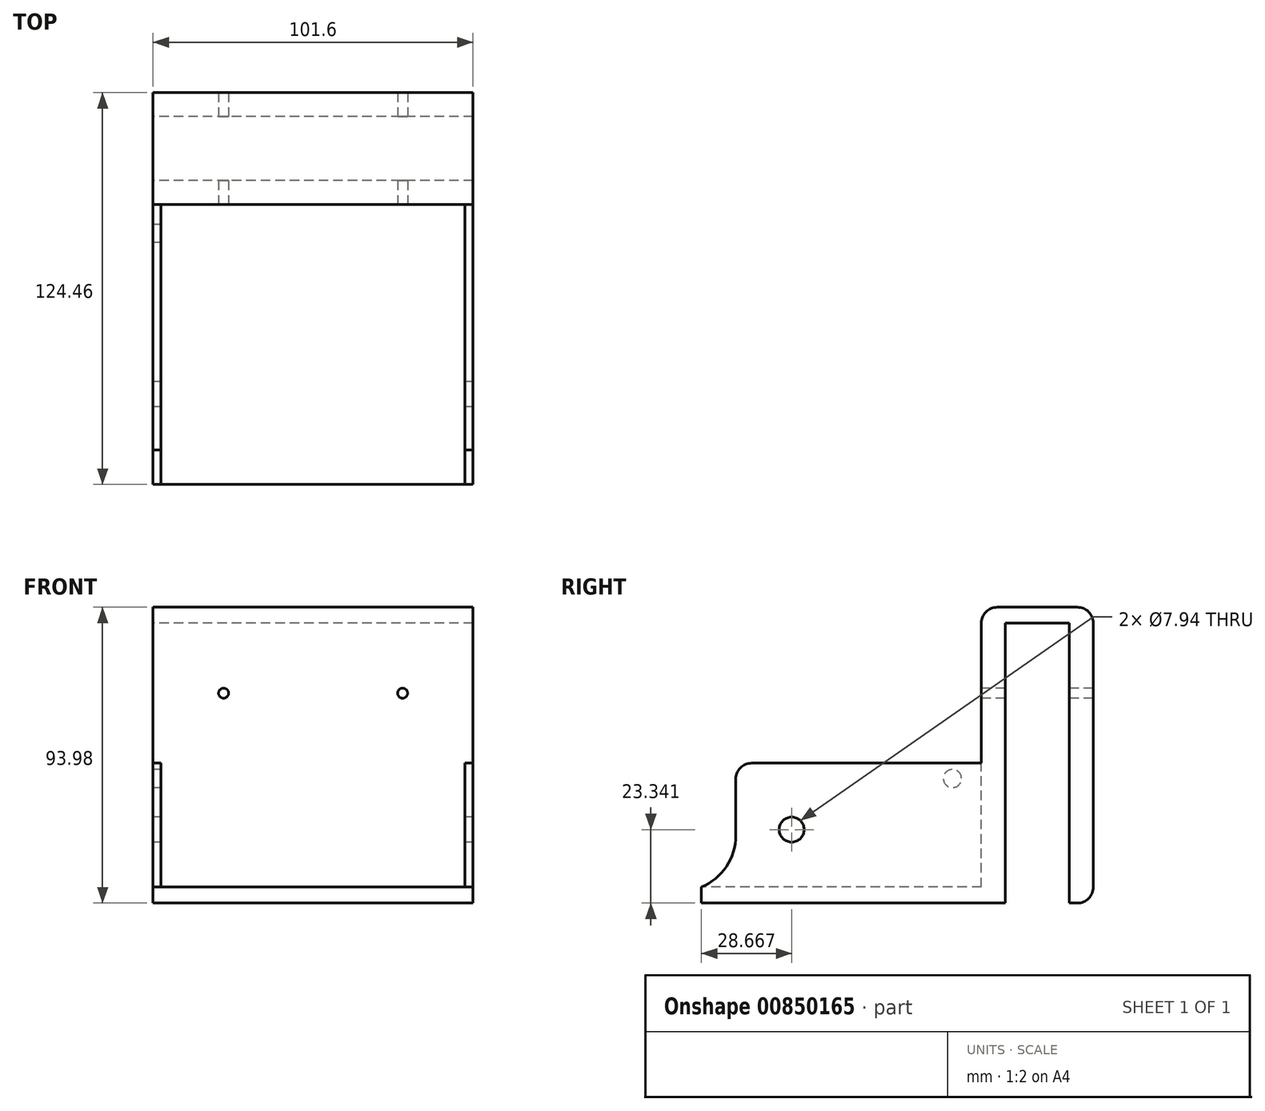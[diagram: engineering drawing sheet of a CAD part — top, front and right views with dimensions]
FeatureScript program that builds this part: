
annotation { "Feature Type Name" : "Feature", "Feature Type Description" : "" }
export const myFeature = defineFeature(function(context is Context, id is Id, definition is map)
    precondition{}
    {
        {
            var Q0;
            Q0=qCreatedBy(makeId("Right.planeOp"),FACE);
            var sketch = newSketch(context, id + "F0", { "sketchPlane" : qUnion([Q0])});
            skLineSegment(sketch, "E0.bottom", {"start": v(-10.16, -44.45) * mm, "end": v(10.16, -44.45) * mm});
            skLineSegment(sketch, "E0.top", {"start": v(-10.16, 44.45) * mm, "end": v(10.16, 44.45) * mm});
            skLineSegment(sketch, "E0.left", {"start": v(-10.16, -44.45) * mm, "end": v(-10.16, 44.45) * mm});
            skLineSegment(sketch, "E0.right", {"start": v(10.16, -44.45) * mm, "end": v(10.16, 44.45) * mm});
            skPoint(sketch, "E0.middle", {"position": v(0, 0) * mm});
            skLineSegment(sketch, "E1.bottom", {"start": v(-17.78, -44.45) * mm, "end": v(17.78, -44.45) * mm});
            skLineSegment(sketch, "E1.top", {"start": v(-17.78, 44.45) * mm, "end": v(17.78, 44.45) * mm});
            skLineSegment(sketch, "E1.left", {"start": v(-17.78, -44.45) * mm, "end": v(-17.78, 44.45) * mm});
            skLineSegment(sketch, "E1.right", {"start": v(17.78, -44.45) * mm, "end": v(17.78, 44.45) * mm});
            skLineSegment(sketch, "E2.top", {"start": v(-17.78, 49.53) * mm, "end": v(17.78, 49.53) * mm});
            skLineSegment(sketch, "E2.left", {"start": v(-17.78, 44.45) * mm, "end": v(-17.78, 49.53) * mm});
            skLineSegment(sketch, "E2.right", {"start": v(17.78, 44.45) * mm, "end": v(17.78, 49.53) * mm});
            skLineSegment(sketch, "E3.bottom", {"start": v(-10.16, -44.45) * mm, "end": v(-106.68, -44.45) * mm});
            skLineSegment(sketch, "E3.top", {"start": v(-10.16, -39.37) * mm, "end": v(-106.68, -39.37) * mm});
            skLineSegment(sketch, "E3.left", {"start": v(-10.16, -44.45) * mm, "end": v(-10.16, -39.37) * mm});
            skLineSegment(sketch, "E3.right", {"start": v(-106.68, -44.45) * mm, "end": v(-106.68, -39.37) * mm});
            skSolve(sketch);
        }
        {
            var Q0;
            {var subQ0=sQuery(id+"F0.wireOp",EDGE,"E0.right");Q0=makeQuery(id+"F0.imprint","IMPRINT",FACE,{"disambiguationData":[TD([[makeQuery(id+"F0.imprint","IMPRINT",EDGE,{"derivedFrom":subQ0}),-1.0]])]});}
            var Q1;
            {var subQ1=sQuery(id+"F0.wireOp",EDGE,"E0.top");Q1=makeQuery(id+"F0.imprint","IMPRINT",FACE,{"disambiguationData":[TD([[makeQuery(id+"F0.imprint","IMPRINT",EDGE,{"derivedFrom":subQ1}),1.0]])]});}
            var Q2;
            {var subQ1=sQuery(id+"F0.wireOp",EDGE,"E0.left");var subQ3=sQuery(id+"F0.wireOp",EDGE,"E3.top");var subQ4=makeQuery(id+"F0.imprint","INTERSECT",VERTEX,{"derivedFrom":[subQ1,subQ3]});Q2=makeQuery(id+"F0.imprint","IMPRINT",FACE,{"disambiguationData":[TD([[makeQuery(id+"F0.imprint","IMPRINT",EDGE,{"disambiguationData":[TD([[subQ4,-1.0]])],"derivedFrom":subQ3}),-1.0]])]});}
            var Q3;
            {var subQ3=sQuery(id+"F0.wireOp",EDGE,"E3.bottom");Q3=makeQuery(id+"F0.imprint","IMPRINT",FACE,{"disambiguationData":[TD([[makeQuery(id+"F0.imprint","IMPRINT",EDGE,{"derivedFrom":subQ3}),-1.0]])]});}
            var Q4;
            {var subQ1=sQuery(id+"F0.wireOp",EDGE,"E0.left");var subQ3=sQuery(id+"F0.wireOp",EDGE,"E3.top");var subQ4=makeQuery(id+"F0.imprint","INTERSECT",VERTEX,{"derivedFrom":[subQ1,subQ3]});Q4=makeQuery(id+"F0.imprint","IMPRINT",FACE,{"disambiguationData":[TD([[makeQuery(id+"F0.imprint","IMPRINT",EDGE,{"disambiguationData":[TD([[subQ4,-1.0]])],"derivedFrom":subQ3}),1.0]])]});}
            extrude(context, id + "F1", {"entities" : qUnion([Q0, Q1, Q2, Q3, Q4]), "depth" : 101.6 * mm, "offsetDistance" : 25.4 * mm});
        }
        {
            var Q0;
            Q0=qCreatedBy(makeId("Front.planeOp"),FACE);
            var sketch = newSketch(context, id + "F2", { "sketchPlane" : qUnion([Q0])});
            skLineSegment(sketch, "E4.0", {"start": v(0, -39.37) * mm, "end": v(0, 49.53) * mm});
            skPoint(sketch, "E5.0", {"position": v(0, 0) * mm});
            skLineSegment(sketch, "E6.0", {"start": v(101.6, -39.37) * mm, "end": v(101.6, 49.53) * mm});
            skLineSegment(sketch, "E7", {"start": v(0, 0) * mm, "end": v(101.6, 0) * mm});
            skPoint(sketch, "E8.0", {"position": v(0, -44.45) * mm});
            skPoint(sketch, "E9.0", {"position": v(101.6, -44.45) * mm});
            skLineSegment(sketch, "E10.bottom", {"start": v(0, 0) * mm, "end": v(2.54, 0) * mm});
            skLineSegment(sketch, "E10.top", {"start": v(0, -44.45) * mm, "end": v(2.54, -44.45) * mm});
            skLineSegment(sketch, "E10.left", {"start": v(0, 0) * mm, "end": v(0, -44.45) * mm});
            skLineSegment(sketch, "E10.right", {"start": v(2.54, 0) * mm, "end": v(2.54, -44.45) * mm});
            skLineSegment(sketch, "E11.bottom", {"start": v(101.6, 0) * mm, "end": v(99.06, 0) * mm});
            skLineSegment(sketch, "E11.top", {"start": v(101.6, -44.45) * mm, "end": v(99.06, -44.45) * mm});
            skLineSegment(sketch, "E11.left", {"start": v(101.6, 0) * mm, "end": v(101.6, -44.45) * mm});
            skLineSegment(sketch, "E11.right", {"start": v(99.06, 0) * mm, "end": v(99.06, -44.45) * mm});
            skSolve(sketch);
        }
        {
            var Q0;
            {Q0=qUnion([makeQuery(id+"F2.imprint","IMPRINT",FACE,{"disambiguationData":[TD([[makeQuery(id+"F2.imprint","IMPRINT",EDGE,{"derivedFrom":sQuery(id+"F2.wireOp",EDGE,"E10.top")}),1.0]])]}),makeQuery(id+"F2.imprint","IMPRINT",FACE,{"disambiguationData":[TD([[makeQuery(id+"F2.imprint","IMPRINT",EDGE,{"derivedFrom":sQuery(id+"F2.wireOp",EDGE,"E11.top")}),-1.0]])]})]);}
            extrude(context, id + "F3", {"entities" : qUnion([Q0]), "operationType" : NewBodyOperationType.ADD, "depth" : 95.76 * mm, "offsetDistance" : 25.4 * mm, "hasSecondDirection" : true, "secondDirectionOppositeDirection" : false, "secondDirectionDepth" : 17.02 * mm});
        }
        {
            var Q0;
            Q0=makeQuery(id+"F3.boolean.opBoolean","INTERSECT",EDGE,{"derivedFrom":[makeQuery(id+"F1.opExtrude","SWEPT_FACE",FACE,{"disambiguationData":[OSD([sQuery(id+"F0.wireOp",EDGE,"E3.top")])]}),makeQuery(id+"F3.opExtrude","CAP_FACE",FACE,{"disambiguationData":[OSD([sQuery(id+"F2.wireOp",EDGE,"E6.0"),sQuery(id+"F2.wireOp",EDGE,"E7"),sQuery(id+"F2.wireOp",EDGE,"E11.top"),sQuery(id+"F2.wireOp",EDGE,"E11.left"),sQuery(id+"F2.wireOp",EDGE,"E11.right")])],"isStart":false})]});
            var Q1;
            Q1=makeQuery(id+"F3.boolean.opBoolean","INTERSECT",EDGE,{"derivedFrom":[makeQuery(id+"F1.opExtrude","SWEPT_FACE",FACE,{"disambiguationData":[OSD([sQuery(id+"F0.wireOp",EDGE,"E3.top")])]}),makeQuery(id+"F3.opExtrude","CAP_FACE",FACE,{"disambiguationData":[OSD([sQuery(id+"F2.wireOp",EDGE,"E4.0"),sQuery(id+"F2.wireOp",EDGE,"E7"),sQuery(id+"F2.wireOp",EDGE,"E10.top"),sQuery(id+"F2.wireOp",EDGE,"E10.left"),sQuery(id+"F2.wireOp",EDGE,"E10.right")])],"isStart":false})]});
            fillet(context, id + "F4", {"entities" : qUnion([Q0, Q1]), "radius" : 17.78 * mm, "tangentPropagation" : true, "allowEdgeOverflow" : false});
        }
        {
            var Q0;
            {var subQ0=sQuery(id+"F2.wireOp",EDGE,"E7");Q0=makeQuery(id+"F3.opExtrude","CAP_EDGE",EDGE,{"disambiguationData":[OSD([subQ0]),TDD([makeQuery(id+"F2.imprint","IMPRINT",EDGE,{"disambiguationData":[TD([[makeQuery(id+"F2.imprint","INTERSECT",VERTEX,{"derivedFrom":[sQuery(id+"F2.wireOp",EDGE,"E4.0"),subQ0]}),-1.0]])],"derivedFrom":subQ0})])],"isStart":false});}
            var Q1;
            {var subQ0=sQuery(id+"F2.wireOp",EDGE,"E7");Q1=makeQuery(id+"F3.opExtrude","CAP_EDGE",EDGE,{"disambiguationData":[OSD([subQ0]),TDD([makeQuery(id+"F2.imprint","IMPRINT",EDGE,{"disambiguationData":[TD([[makeQuery(id+"F2.imprint","INTERSECT",VERTEX,{"derivedFrom":[sQuery(id+"F2.wireOp",EDGE,"E6.0"),subQ0]}),1.0]])],"derivedFrom":subQ0})])],"isStart":false});}
            fillet(context, id + "F5", {"entities" : qUnion([Q0, Q1]), "radius" : 5.08 * mm, "tangentPropagation" : true, "allowEdgeOverflow" : false});
        }
        {
            var Q0;
            Q0=makeQuery(id+"F1.opExtrude","SWEPT_EDGE",EDGE,{"disambiguationData":[OSD([sQuery(id+"F0.wireOp",EDGE,"E2.top"),sQuery(id+"F0.wireOp",EDGE,"E2.left")])]});
            var Q1;
            Q1=makeQuery(id+"F1.opExtrude","SWEPT_EDGE",EDGE,{"disambiguationData":[OSD([sQuery(id+"F0.wireOp",EDGE,"E2.top"),sQuery(id+"F0.wireOp",EDGE,"E2.right")])]});
            fillet(context, id + "F6", {"entities" : qUnion([Q0, Q1]), "radius" : 5.08 * mm, "tangentPropagation" : true, "allowEdgeOverflow" : false});
        }
        {
            var Q0;
            Q0=makeQuery(id+"F1.opExtrude","SWEPT_EDGE",EDGE,{"disambiguationData":[OSD([sQuery(id+"F0.wireOp",EDGE,"E1.bottom"),sQuery(id+"F0.wireOp",EDGE,"E1.right")])]});
            fillet(context, id + "F7", {"entities" : qUnion([Q0]), "radius" : 5.08 * mm, "tangentPropagation" : true, "allowEdgeOverflow" : false});
        }
        {
            var Q0;
            Q0=qCreatedBy(makeId("Right.planeOp"),FACE);
            var sketch = newSketch(context, id + "F8", { "sketchPlane" : qUnion([Q0])});
            skCircle(sketch, "E12", {"center": v(-78.01, -21.1) * mm, "radius": 3.97 * mm});
            skSolve(sketch);
        }
        {
            var Q0;
            Q0 = qSketchRegion(id + "F8", true);
            extrude(context, id + "F9", {"entities" : qUnion([Q0]), "operationType" : NewBodyOperationType.REMOVE, "depth" : 154.7 * mm, "offsetDistance" : 25.4 * mm});
        }
        {
            var Q0;
            Q0=qCreatedBy(makeId("Right.planeOp"),FACE);
            var sketch = newSketch(context, id + "F10", { "sketchPlane" : qUnion([Q0])});
            skCircle(sketch, "E13", {"center": v(-26.95, -4.89) * mm, "radius": 2.88 * mm});
            skSolve(sketch);
        }
        {
            var Q0;
            Q0 = qSketchRegion(id + "F10", true);
            extrude(context, id + "F11", {"entities" : qUnion([Q0]), "operationType" : NewBodyOperationType.REMOVE, "depth" : 33.78 * mm, "offsetDistance" : 25.4 * mm});
        }
        {
            var Q0;
            Q0=makeQuery(id+"F1.opExtrude","SWEPT_FACE",FACE,{"disambiguationData":[OSD([sQuery(id+"F0.wireOp",EDGE,"E1.left"),sQuery(id+"F0.wireOp",EDGE,"E2.left")])]});
            var sketch = newSketch(context, id + "F12", { "sketchPlane" : qUnion([Q0])});
            skPoint(sketch, "E14.0", {"position": v(0, 22.23) * mm});
            skPoint(sketch, "E15.0", {"position": v(101.6, 22.23) * mm});
            skLineSegment(sketch, "E16.left", {"start": v(22.38, 22.23) * mm, "end": v(22.38, 22.23) * mm});
            skLineSegment(sketch, "E16.right", {"start": v(79.22, 22.23) * mm, "end": v(79.22, 22.23) * mm});
            skPoint(sketch, "E16.middle", {"position": v(50.8, 22.23) * mm});
            skCircle(sketch, "E17", {"center": v(22.38, 22.23) * mm, "radius": 1.59 * mm});
            skCircle(sketch, "E18", {"center": v(79.22, 22.23) * mm, "radius": 1.59 * mm});
            skSolve(sketch);
        }
        {
            var Q0;
            Q0 = qSketchRegion(id + "F12", true);
            extrude(context, id + "F13", {"entities" : qUnion([Q0]), "operationType" : NewBodyOperationType.REMOVE, "oppositeDirection" : true, "depth" : 85.34 * mm, "offsetDistance" : 25.4 * mm});
        }
    });
